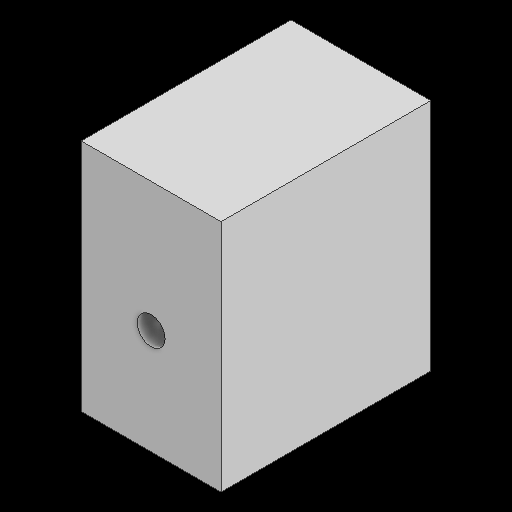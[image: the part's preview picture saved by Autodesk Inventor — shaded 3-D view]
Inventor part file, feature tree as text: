
AUTODESK INVENTOR PART (.ipt)
format: ipt  version: 2025.1 (Build 291241000, 241)  size: 92,160 bytes
history: native  units: in
note: dims shown in document units (in); Inventor stores cm internally (conversion verified against a paired STEP export)
features: extrude x2, sketch x2, other x1
ambient origin geometry x8: Origin, YZ Plane, XZ Plane, XY Plane, X Axis, Y Axis, Z Axis, Center Point
bodies: Body1 (feature_tree)
feature tree (5):
  other  "솔리드1"
  extrude  "돌출1"  Depth=1.3189in
  extrude  "돌출2"  Depth=0.7874in
  sketch  "스케치1"
  sketch  "스케치2"
